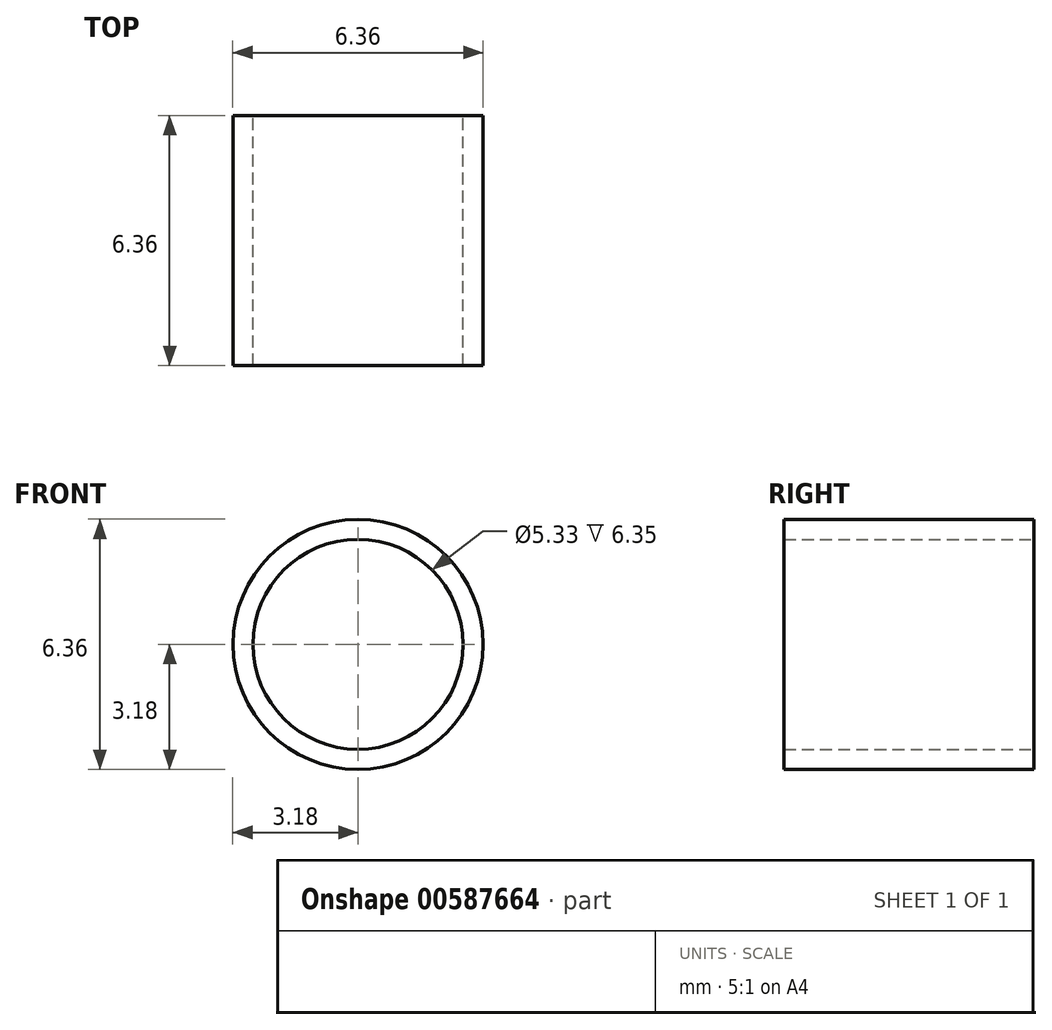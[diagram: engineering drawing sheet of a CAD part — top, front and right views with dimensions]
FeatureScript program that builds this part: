
annotation { "Feature Type Name" : "Feature", "Feature Type Description" : "" }
export const myFeature = defineFeature(function(context is Context, id is Id, definition is map)
    precondition{}
    {
        {
            var Q0;
            Q0=qCreatedBy(makeId("Front.planeOp"),FACE);
            var sketch = newSketch(context, id + "F0", { "sketchPlane" : qUnion([Q0])});
            skCircle(sketch, "E0", {"center": v(0, 0) * mm, "radius": 3.18 * mm});
            skCircle(sketch, "E1", {"center": v(0, 0) * mm, "radius": 2.67 * mm});
            skSolve(sketch);
        }
        {
            var Q0;
            Q0 = qSketchRegion(id + "F0", true);
            extrude(context, id + "F1", {"entities" : qUnion([Q0]), "endBound" : BoundingType.SYMMETRIC, "depth" : 6.35 * mm, "offsetDistance" : 25.4 * mm});
        }
    });
